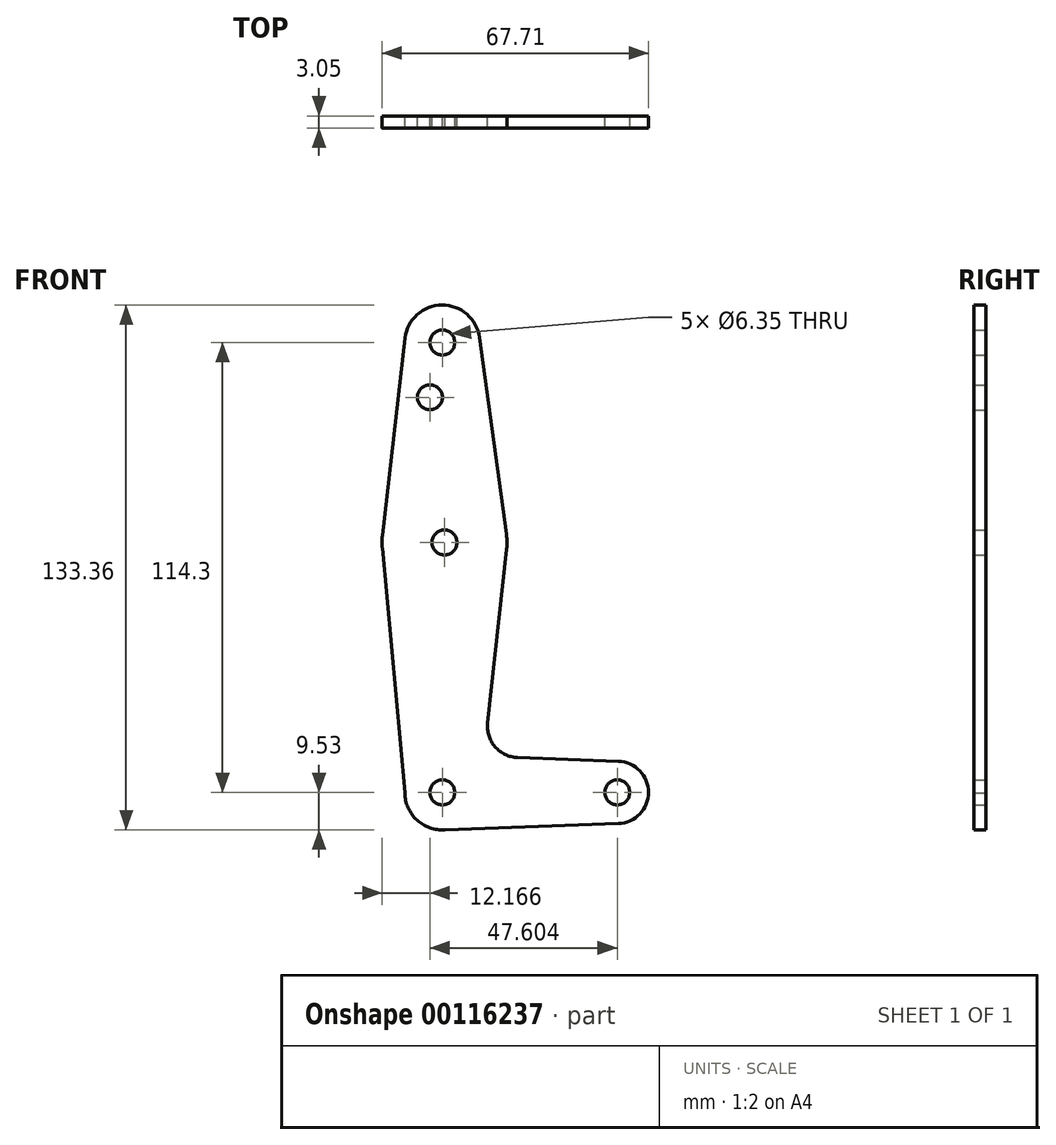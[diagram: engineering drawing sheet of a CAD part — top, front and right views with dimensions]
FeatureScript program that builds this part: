
annotation { "Feature Type Name" : "Feature", "Feature Type Description" : "" }
export const myFeature = defineFeature(function(context is Context, id is Id, definition is map)
    precondition{}
    {
        {
            var Q0;
            Q0=qCreatedBy(makeId("Front.planeOp"),FACE);
            var sketch = newSketch(context, id + "F0", { "sketchPlane" : qUnion([Q0])});
            skLineSegment(sketch, "E0", {"start": v(0, 0) * mm, "end": v(44.45, 0) * mm});
            skCircle(sketch, "E1", {"center": v(0, 114.3) * mm, "radius": 9.53 * mm});
            skCircle(sketch, "E2", {"center": v(44.45, 0) * mm, "radius": 7.94 * mm});
            skCircle(sketch, "E3", {"center": v(0, 0) * mm, "radius": 9.53 * mm});
            skCircle(sketch, "E4", {"center": v(0.55, 63.5) * mm, "radius": 15.88 * mm});
            skLineSegment(sketch, "E5", {"start": v(0, 0) * mm, "end": v(44.45, 0) * mm, "construction": true});
            skLineSegment(sketch, "E6", {"start": v(0, 114.3) * mm, "end": v(0, 0) * mm, "construction": true});
            skLineSegment(sketch, "E7", {"start": v(-9.46, 115.39) * mm, "end": v(-15.22, 65.31) * mm});
            skLineSegment(sketch, "E8", {"start": v(9.44, 115.6) * mm, "end": v(16.28, 65.66) * mm});
            skLineSegment(sketch, "E9", {"start": v(16.34, 61.77) * mm, "end": v(11.51, 17.65) * mm});
            skLineSegment(sketch, "E10", {"start": v(19.13, 8.84) * mm, "end": v(44.73, 7.93) * mm});
            skLineSegment(sketch, "E11", {"start": v(0, -9.53) * mm, "end": v(44.73, -7.93) * mm});
            skCircle(sketch, "E12", {"center": v(0, 0) * mm, "radius": 3.18 * mm});
            skCircle(sketch, "E13", {"center": v(44.45, 0) * mm, "radius": 3.18 * mm});
            skCircle(sketch, "E14", {"center": v(0.55, 63.5) * mm, "radius": 3.18 * mm});
            skCircle(sketch, "E15", {"center": v(0, 114.3) * mm, "radius": 3.18 * mm});
            skLineSegment(sketch, "E16", {"start": v(0, 100.03) * mm, "end": v(-3.15, 100.39) * mm, "construction": true});
            skCircle(sketch, "E17", {"center": v(-3.15, 100.39) * mm, "radius": 3.18 * mm});
            skArc(sketch, "E18.filletArc", {"start": v(11.51, 17.65) * mm, "mid": v(13.4, 11.59) * mm, "end": v(19.13, 8.84) * mm});
            skLineSegment(sketch, "E19", {"start": v(-9.39, -1.6) * mm, "end": v(-15.25, 62.04) * mm});
            skSolve(sketch);
        }
        {
            var Q0;
            Q0 = qSketchRegion(id + "F0", true);
            extrude(context, id + "F1", {"entities" : qUnion([Q0]), "depth" : 3.05 * mm});
        }
    });
